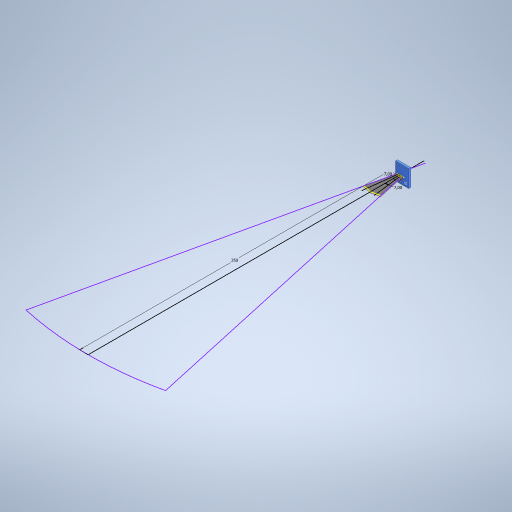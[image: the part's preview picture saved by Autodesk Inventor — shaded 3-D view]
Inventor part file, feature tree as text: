
AUTODESK INVENTOR PART (.ipt)
format: ipt  version: 2023 (Build 270158000, 158)  size: 366,592 bytes
history: native  units: in
note: dims shown in document units (in); Inventor stores cm internally (conversion verified against a paired STEP export)
features: sketch x6, extrude x5, projected_geometry x4
ambient origin geometry x8: Origin, YZ Plane, XZ Plane, XY Plane, X Axis, Y Axis, Z Axis, Center Point
bodies: Solid1 (feature_tree)
feature tree (15):
  sketch  "Sketch1"  dims[d0=0.4213in d1=0.5512in]
  extrude  "Extrusion1"  Depth=0.5512in
  extrude  "Extrusion2"  Depth=0.0394in
  extrude  "Extrusion3"  Depth=0.1732in
  extrude  "Extrusion4"  Depth=0.0433in TaperAngle=0.0deg
  extrude  "Wyciągnięcie proste5"  Depth=0.0394in
  sketch  "Szkic5"
  sketch  "Szkic6"
  sketch  "Sketch2"  dims[d2=0.1378in d3=0.0394in]
  projected_geometry  "Projected Loop1"
  sketch  "Sketch3"  dims[d4=0.0945in d5=0.1732in]
  projected_geometry  "Projected Loop2"
  sketch  "Sketch4"  dims[d6=0.063in d7=0.0in d8=0.0433in d9=0.0in d10=0.0394in d11=0.0394in d12=0.2598in d13=0.0in d14=0.0in d15=0.0394in d16=0.0394in d17=0.0433in d18=1.5748in d20=0.1in d21=0.3937in d23=0.3937in d25=0.0394in d26=0.0394in d27=0.0433in d28=0.7874in d30=0.1in d31=0.3937in d33=0.3937in d35=0.0in d36=0.0in d37=0.0859in d38=0.0859in d39=0.0394in d40=0.0in d41=9.8425in d42=0.0481in d43=0.0481in]
  projected_geometry  "Projected Loop3"
  projected_geometry  "Pętla rzutowana4"
